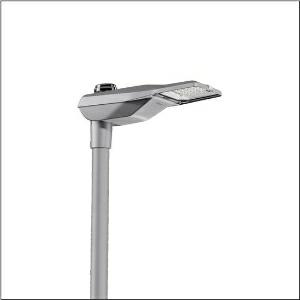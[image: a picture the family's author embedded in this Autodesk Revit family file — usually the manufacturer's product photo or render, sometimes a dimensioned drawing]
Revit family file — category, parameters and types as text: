
# Revit family: streetlight_sl_21_micro___stw1_0a_5xe5e37n08cb_b20b
name_source: partatom
category: Lighting Fixtures
units: mm (PartAtom-declared; Revit-internal decimal feet)

## family parameters
Cut with Voids When Loaded = No
Host = Face
Light Source = No
Part Type = Normal
Room Calculation Point = No
Round Connector Dimension = Use Diameter
Shared = No

## types (1)
- --- (1 x LED, 2290 lm, 15.8 W, 3000K)
    Apparent Load = 16 VA
    CIE Flux Codes = 38 75 98 100 100
    Color Rendering = 70
    Color Temperature = 3000K
    Default Elevation = 1800 mm
    Description = Streetlight SL 21 micro, mast luminaire, primary light control with lens, of PMMA, primary optical cover: cover, of toughened safety glass, transparent, light distribution: STW1.0a, light emission: direct distribution, primary light characteristic: asymmetric, installation type: post-top, LED, 3G 1.5mm², High Power LED, rated luminous flux: 2.290lm, luminous efficacy: 145lm/W, light colour: 730, colour temperature: 3000K, control gear: NEMA (7pin), control: overheat protection, pre-setting: linear dimming characteristic, constant luminous flux control, time-dependent luminous flux control, flexible luminous flux parameterisation, mains connection: 230..240V, AC, 50/60Hz, connection cable pre-assembled, cable length: 6,5m, wiring characteristics: H07RN-F, start of lifetime: 16W, end of service life: 16W, reduction: 8W, luminaire housing, of diecast aluminium (EN AC-44300), powder-coated, Siteco® metallic grey (DB 702S), corrosivity category C5 mid according to DIN EN ISO 12944, multi-level sealing system, sealing non-destructively replaceable, inclination adjustable: 0°, 5°, 10°, 15°, length: 528mm, width: 235mm, height: 110mm, spigot size: 76/60mm (post-top), mounting height: 4..8m, protection rating (complete): IP66, insulation class (complete): insulation class I (protective earthing), certification: CE, ENEC, ENEC+, VDE, impact resistance: IK10, permissible operating ambient temperature for outdoor applications: -40..+50°C, standard-compliant lighting for roads and squares, packaging unit: 1 piece

Light Distribution: STW1.0a
    Height = 110 mm
    Lamp = 1 x LED
    Lamp Light Flux = 2290 lm
    Lamp Power = 15.8 W
    Lamp count = 1
    Length = 528 mm
    Luminous efficacy = 145 lm/W
    Manufacturer = Siteco
    ModVariant = No
    Model = 5XE5E37N08CB
    Number of Poles = 1
    OnlyDefault = Yes
    Power Factor = 1
    Product Name = Streetlight SL 21 micro | STW1.0a
    Product group = mast luminaire | pylon top
    ProductGroupID = 6100
    Protection Class = Protection class I
    Protection Degree = IP 66
    RLX_Detail_Level = 1
    RLX_Emergency_Light_Flux = 0 lm
    RLX_Emergency_Type = 0
    RLX_Emergency_Type_DB = No
    RlxData = <blob elided: 98373 chars, md5=0c1388f6>
    Socket = socket
    Standby Power = 0 W
    System Light Flux = 2290 lm
    System Power = 16 W
    Type Comments = factory setting: luminous flux: 100 % | dim-lin: 254 | 300 mA
    Type Image = l_1294375.jpg
    URL = http://relux.com
    VarID = @adj_157341
    Voltage = 0 V
    Weight = 0.00 kg
    Width = 235 mm

## geometry (parser evidence)
native form markers: Blend x4, Sweep x9
no freeform markers — native parametric forms only
